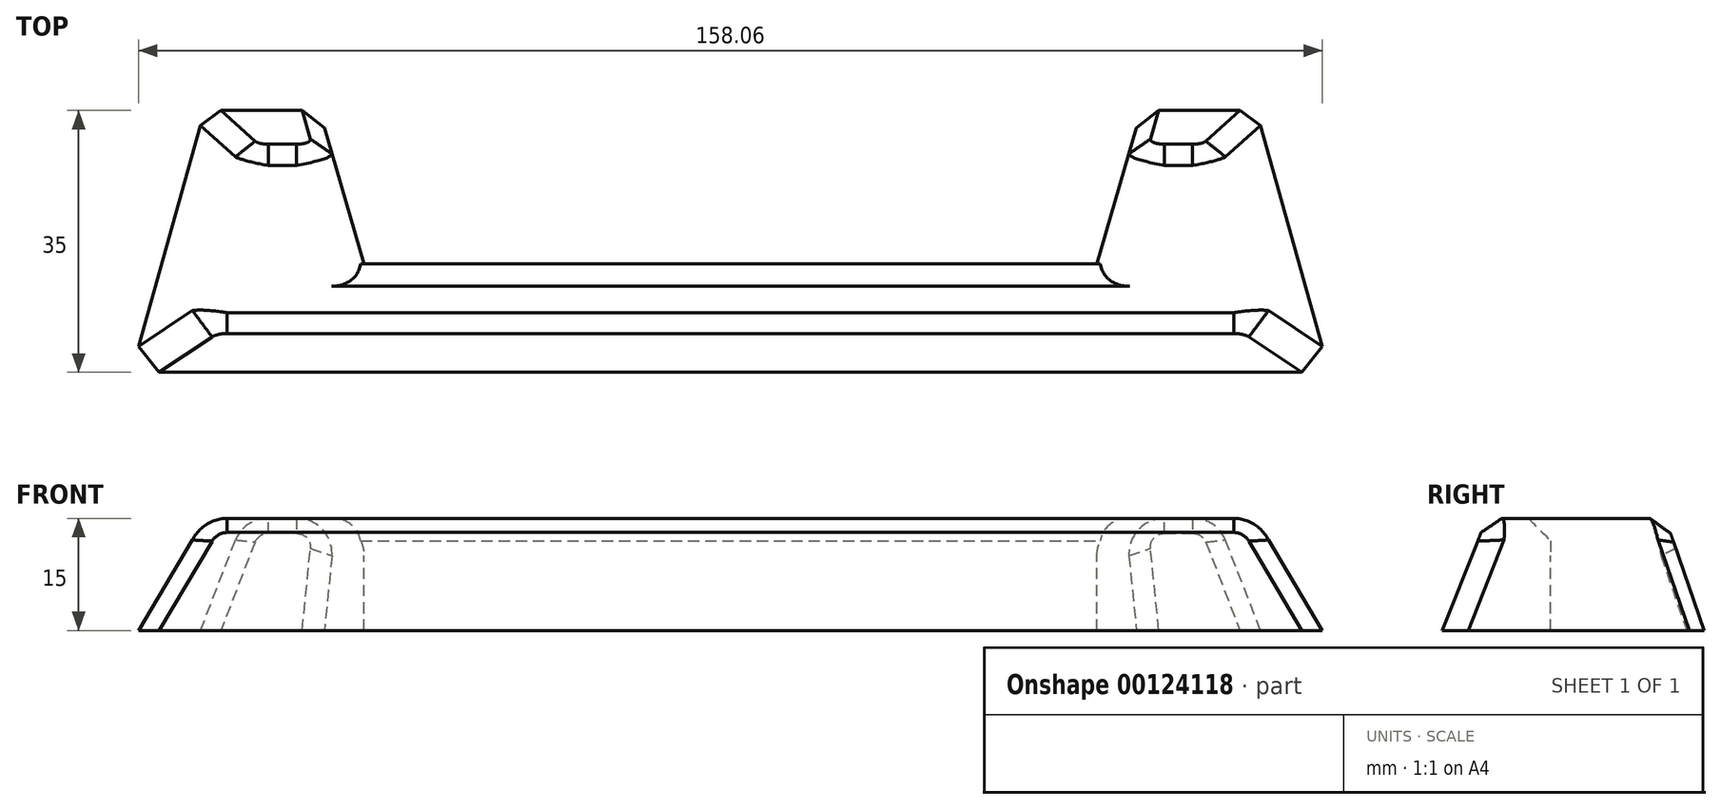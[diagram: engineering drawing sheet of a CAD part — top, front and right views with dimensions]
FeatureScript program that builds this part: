
annotation { "Feature Type Name" : "Feature", "Feature Type Description" : "" }
export const myFeature = defineFeature(function(context is Context, id is Id, definition is map)
    precondition{}
    {
        {
            var Q0;
            Q0=qCreatedBy(makeId("Top.planeOp"),FACE);
            var sketch = newSketch(context, id + "F0", { "sketchPlane" : qUnion([Q0])});
            skLineSegment(sketch, "E0", {"start": v(0, -14.5) * mm, "end": v(80, -14.5) * mm});
            skLineSegment(sketch, "E1", {"start": v(80, -14.5) * mm, "end": v(70.21, 20.5) * mm});
            skLineSegment(sketch, "E2", {"start": v(70.21, 20.5) * mm, "end": v(54.9, 20.5) * mm});
            skLineSegment(sketch, "E3", {"start": v(54.9, 20.5) * mm, "end": v(48.94, 0) * mm});
            skLineSegment(sketch, "E4", {"start": v(48.94, 0) * mm, "end": v(-31.06, 0) * mm});
            skLineSegment(sketch, "E5.MirrorCS", {"start": v(0, -14.5) * mm, "end": v(-80, -14.5) * mm});
            skLineSegment(sketch, "E6.MirrorCS", {"start": v(-80, -14.5) * mm, "end": v(-70.21, 20.5) * mm});
            skLineSegment(sketch, "E7.MirrorCS", {"start": v(-70.21, 20.5) * mm, "end": v(-54.9, 20.5) * mm});
            skLineSegment(sketch, "E8.MirrorCS", {"start": v(-48.94, 0) * mm, "end": v(0, 0) * mm});
            skLineSegment(sketch, "E9.MirrorCS", {"start": v(-54.9, 20.5) * mm, "end": v(-48.94, 0) * mm});
            skSolve(sketch);
        }
        {
            var Q0;
            Q0=qCreatedBy(makeId("Top.planeOp"),FACE);
            cPlane(context, id + "F1", {"entities" : qUnion([Q0]), "cplaneType" : CPlaneType.OFFSET, "offset" : 15 * mm, "width" : 152.4 * mm, "height" : 152.4 * mm});
        }
        {
            var Q0;
            Q0=qCreatedBy(id+"F1.planeOp",FACE);
            var sketch = newSketch(context, id + "F2", { "sketchPlane" : qUnion([Q0])});
            skLineSegment(sketch, "E10.3", {"start": v(53.38, 15.3) * mm, "end": v(48.94, 0) * mm});
            skLineSegment(sketch, "E10.4", {"start": v(48.94, 0) * mm, "end": v(0, 0) * mm});
            skLineSegment(sketch, "E11.2", {"start": v(64.42, 15.3) * mm, "end": v(53.38, 15.3) * mm});
            skLineSegment(sketch, "E11.3", {"start": v(71.09, -8.55) * mm, "end": v(64.42, 15.3) * mm});
            skPoint(sketch, "E10.7.end.orphan", {"position": v(-54.9, 20.5) * mm});
            skPoint(sketch, "E10.7.start.orphan", {"position": v(-70.21, 20.5) * mm});
            skPoint(sketch, "E10.8.end.orphan", {"position": v(-70.21, 20.5) * mm});
            skPoint(sketch, "E10.8.start.orphan", {"position": v(-80, -14.5) * mm});
            skPoint(sketch, "E10.9.end.orphan", {"position": v(-80, -14.5) * mm});
            skPoint(sketch, "E10.9.start.orphan", {"position": v(0, -14.5) * mm});
            skPoint(sketch, "E10.0.end.orphan", {"position": v(80, -14.5) * mm});
            skPoint(sketch, "E10.0.start.orphan", {"position": v(0, -14.5) * mm});
            skPoint(sketch, "E10.2.end.orphan", {"position": v(70.21, 20.5) * mm});
            skPoint(sketch, "E10.2.start.orphan", {"position": v(80, -14.5) * mm});
            skPoint(sketch, "E10.1.end.orphan", {"position": v(54.9, 20.5) * mm});
            skPoint(sketch, "E10.1.start.orphan", {"position": v(70.21, 20.5) * mm});
            skPoint(sketch, "E12.orphan", {"position": v(0, 0) * mm});
            skPoint(sketch, "E10.6.start.orphan", {"position": v(-48.94, 0) * mm});
            skPoint(sketch, "E13.orphan", {"position": v(-31.06, 0) * mm});
            skPoint(sketch, "E10.5.start.orphan", {"position": v(-54.9, 20.5) * mm});
            skLineSegment(sketch, "E14", {"start": v(71.09, -8.55) * mm, "end": v(0, -8.55) * mm});
            skLineSegment(sketch, "E15.MirrorCS", {"start": v(-71.09, -8.55) * mm, "end": v(0, -8.55) * mm});
            skLineSegment(sketch, "E16.MirrorCS", {"start": v(-71.09, -8.55) * mm, "end": v(-64.42, 15.3) * mm});
            skLineSegment(sketch, "E17.MirrorCS", {"start": v(-64.42, 15.3) * mm, "end": v(-53.38, 15.3) * mm});
            skLineSegment(sketch, "E18.MirrorCS", {"start": v(-48.94, 0) * mm, "end": v(0, 0) * mm});
            skLineSegment(sketch, "E19.MirrorCS", {"start": v(-53.38, 15.3) * mm, "end": v(-48.94, 0) * mm});
            skSolve(sketch);
        }
        {
            var Q0;
            Q0=makeQuery(id+"F0.imprint","IMPRINT",FACE,{"disambiguationData":[TD([[makeQuery(id+"F0.imprint","IMPRINT",EDGE,{"derivedFrom":sQuery(id+"F0.wireOp",EDGE,"E0")}),1.0]])]});
            var Q1;
            Q1=makeQuery(id+"F2.imprint","IMPRINT",FACE,{"disambiguationData":[TD([[makeQuery(id+"F2.imprint","IMPRINT",EDGE,{"derivedFrom":sQuery(id+"F2.wireOp",EDGE,"E10.3")}),1.0]])]});
            loft(context, id + "F3", {"sheetProfilesArray" : [{ "sheetProfileEntities" : qUnion([Q0]) }, { "sheetProfileEntities" : qUnion([Q1]) }]});
        }
        {
            var Q0;
            Q0=makeQuery(id+"F3.opLoft","MID_CAP_EDGE",EDGE,{"disambiguationData":[OSD([sQuery(id+"F2.wireOp",EDGE,"E15.MirrorCS"),sQuery(id+"F2.wireOp",EDGE,"E16.MirrorCS"),sQuery(id+"F2.wireOp",EDGE,"E17.MirrorCS")])],"capPos":1.0});
            var Q1;
            Q1=makeQuery(id+"F3.opLoft","MID_CAP_EDGE",EDGE,{"disambiguationData":[OSD([sQuery(id+"F2.wireOp",EDGE,"E17.MirrorCS"),sQuery(id+"F2.wireOp",EDGE,"E18.MirrorCS"),sQuery(id+"F2.wireOp",EDGE,"E19.MirrorCS")])],"capPos":1.0});
            var Q2;
            Q2=makeQuery(id+"F3.opLoft","MID_CAP_EDGE",EDGE,{"disambiguationData":[OSD([sQuery(id+"F2.wireOp",EDGE,"E10.3"),sQuery(id+"F2.wireOp",EDGE,"E10.4"),sQuery(id+"F2.wireOp",EDGE,"E11.2")])],"capPos":1.0});
            var Q3;
            Q3=makeQuery(id+"F3.opLoft","MID_CAP_EDGE",EDGE,{"disambiguationData":[OSD([sQuery(id+"F2.wireOp",EDGE,"E11.2"),sQuery(id+"F2.wireOp",EDGE,"E11.3"),sQuery(id+"F2.wireOp",EDGE,"E14")])],"capPos":1.0});
            fillet(context, id + "F4", {"entities" : qUnion([Q0, Q1, Q2, Q3]), "radius" : 5 * mm, "tangentPropagation" : true, "allowEdgeOverflow" : false});
        }
        {
            var Q0;
            Q0=makeQuery(id+"F3.opLoft","MID_CAP_EDGE",EDGE,{"disambiguationData":[OSD([sQuery(id+"F2.wireOp",EDGE,"E10.3"),sQuery(id+"F2.wireOp",EDGE,"E10.4"),sQuery(id+"F2.wireOp",EDGE,"E18.MirrorCS")])],"capPos":1.0});
            var Q1;
            Q1=makeQuery(id+"F3.opLoft","MID_CAP_EDGE",EDGE,{"disambiguationData":[OSD([sQuery(id+"F2.wireOp",EDGE,"E14"),sQuery(id+"F2.wireOp",EDGE,"E15.MirrorCS"),sQuery(id+"F2.wireOp",EDGE,"E16.MirrorCS")])],"capPos":1.0});
            chamfer(context, id + "F5", {"entities" : qUnion([Q0, Q1]), "width" : 3 * mm, "tangentPropagation" : true});
        }
        {
            var Q0;
            Q0=makeQuery(id+"F3.opLoft","SWEPT_EDGE",EDGE,{"disambiguationData":[OSD([sQuery(id+"F0.wireOp",EDGE,"E1"),sQuery(id+"F0.wireOp",EDGE,"E2"),sQuery(id+"F2.wireOp",EDGE,"E11.2"),sQuery(id+"F2.wireOp",EDGE,"E11.3")])]});
            var Q1;
            {var subQ0=sQuery(id+"F2.wireOp",EDGE,"E11.3");var subQ1=sQuery(id+"F2.wireOp",EDGE,"E11.2");Q1=makeQuery(id+"F4.opFillet","BLEND_EDGE",EDGE,{"blendedFrom":[makeQuery(id+"F3.opLoft","MID_CAP_EDGE",EDGE,{"disambiguationData":[OSD([subQ1,subQ0,sQuery(id+"F2.wireOp",EDGE,"E14")])],"capPos":1.0}),makeQuery(id+"F3.opLoft","SWEPT_FACE",FACE,{"disambiguationData":[OSD([sQuery(id+"F0.wireOp",EDGE,"E1"),sQuery(id+"F0.wireOp",EDGE,"E2"),sQuery(id+"F0.wireOp",EDGE,"E3"),sQuery(id+"F2.wireOp",EDGE,"E10.3"),subQ1,subQ0])]})],"blendedInto":[makeQuery(id+"F3.opLoft","SWEPT_FACE",FACE,{"disambiguationData":[OSD([sQuery(id+"F0.wireOp",EDGE,"E1"),sQuery(id+"F0.wireOp",EDGE,"E2"),sQuery(id+"F0.wireOp",EDGE,"E3"),sQuery(id+"F2.wireOp",EDGE,"E10.3"),subQ1,subQ0])]})]});}
            var Q2;
            {var subQ0=sQuery(id+"F2.wireOp",EDGE,"E11.2");var subQ1=sQuery(id+"F2.wireOp",EDGE,"E10.3");Q2=makeQuery(id+"F4.opFillet","BLEND_EDGE",EDGE,{"blendedFrom":[makeQuery(id+"F3.opLoft","MID_CAP_EDGE",EDGE,{"disambiguationData":[OSD([subQ1,sQuery(id+"F2.wireOp",EDGE,"E10.4"),subQ0])],"capPos":1.0}),makeQuery(id+"F3.opLoft","SWEPT_FACE",FACE,{"disambiguationData":[OSD([sQuery(id+"F0.wireOp",EDGE,"E1"),sQuery(id+"F0.wireOp",EDGE,"E2"),sQuery(id+"F0.wireOp",EDGE,"E3"),subQ1,subQ0,sQuery(id+"F2.wireOp",EDGE,"E11.3")])]})],"blendedInto":[makeQuery(id+"F3.opLoft","SWEPT_FACE",FACE,{"disambiguationData":[OSD([sQuery(id+"F0.wireOp",EDGE,"E1"),sQuery(id+"F0.wireOp",EDGE,"E2"),sQuery(id+"F0.wireOp",EDGE,"E3"),subQ1,subQ0,sQuery(id+"F2.wireOp",EDGE,"E11.3")])]})]});}
            var Q3;
            Q3=makeQuery(id+"F3.opLoft","SWEPT_EDGE",EDGE,{"disambiguationData":[OSD([sQuery(id+"F0.wireOp",EDGE,"E2"),sQuery(id+"F0.wireOp",EDGE,"E3"),sQuery(id+"F2.wireOp",EDGE,"E10.3"),sQuery(id+"F2.wireOp",EDGE,"E11.2")])]});
            var Q4;
            Q4=makeQuery(id+"F3.opLoft","MID_CAP_EDGE",EDGE,{"disambiguationData":[OSD([sQuery(id+"F2.wireOp",EDGE,"E10.3"),sQuery(id+"F2.wireOp",EDGE,"E11.2"),sQuery(id+"F2.wireOp",EDGE,"E11.3")])],"capPos":1.0});
            var Q5;
            Q5=makeQuery(id+"F3.opLoft","MID_CAP_EDGE",EDGE,{"disambiguationData":[OSD([sQuery(id+"F2.wireOp",EDGE,"E16.MirrorCS"),sQuery(id+"F2.wireOp",EDGE,"E17.MirrorCS"),sQuery(id+"F2.wireOp",EDGE,"E19.MirrorCS")])],"capPos":1.0});
            var Q6;
            {var subQ0=sQuery(id+"F2.wireOp",EDGE,"E19.MirrorCS");var subQ1=sQuery(id+"F2.wireOp",EDGE,"E17.MirrorCS");Q6=makeQuery(id+"F4.opFillet","BLEND_EDGE",EDGE,{"blendedFrom":[makeQuery(id+"F3.opLoft","MID_CAP_EDGE",EDGE,{"disambiguationData":[OSD([subQ1,sQuery(id+"F2.wireOp",EDGE,"E18.MirrorCS"),subQ0])],"capPos":1.0}),makeQuery(id+"F3.opLoft","SWEPT_FACE",FACE,{"disambiguationData":[OSD([sQuery(id+"F0.wireOp",EDGE,"E6.MirrorCS"),sQuery(id+"F0.wireOp",EDGE,"E7.MirrorCS"),sQuery(id+"F0.wireOp",EDGE,"E9.MirrorCS"),sQuery(id+"F2.wireOp",EDGE,"E16.MirrorCS"),subQ1,subQ0])]})],"blendedInto":[makeQuery(id+"F3.opLoft","SWEPT_FACE",FACE,{"disambiguationData":[OSD([sQuery(id+"F0.wireOp",EDGE,"E6.MirrorCS"),sQuery(id+"F0.wireOp",EDGE,"E7.MirrorCS"),sQuery(id+"F0.wireOp",EDGE,"E9.MirrorCS"),sQuery(id+"F2.wireOp",EDGE,"E16.MirrorCS"),subQ1,subQ0])]})]});}
            var Q7;
            {var subQ0=sQuery(id+"F2.wireOp",EDGE,"E17.MirrorCS");var subQ1=sQuery(id+"F2.wireOp",EDGE,"E16.MirrorCS");Q7=makeQuery(id+"F4.opFillet","BLEND_EDGE",EDGE,{"blendedFrom":[makeQuery(id+"F3.opLoft","MID_CAP_EDGE",EDGE,{"disambiguationData":[OSD([sQuery(id+"F2.wireOp",EDGE,"E15.MirrorCS"),subQ1,subQ0])],"capPos":1.0}),makeQuery(id+"F3.opLoft","SWEPT_FACE",FACE,{"disambiguationData":[OSD([sQuery(id+"F0.wireOp",EDGE,"E6.MirrorCS"),sQuery(id+"F0.wireOp",EDGE,"E7.MirrorCS"),sQuery(id+"F0.wireOp",EDGE,"E9.MirrorCS"),subQ1,subQ0,sQuery(id+"F2.wireOp",EDGE,"E19.MirrorCS")])]})],"blendedInto":[makeQuery(id+"F3.opLoft","SWEPT_FACE",FACE,{"disambiguationData":[OSD([sQuery(id+"F0.wireOp",EDGE,"E6.MirrorCS"),sQuery(id+"F0.wireOp",EDGE,"E7.MirrorCS"),sQuery(id+"F0.wireOp",EDGE,"E9.MirrorCS"),subQ1,subQ0,sQuery(id+"F2.wireOp",EDGE,"E19.MirrorCS")])]})]});}
            var Q8;
            Q8=makeQuery(id+"F3.opLoft","SWEPT_EDGE",EDGE,{"disambiguationData":[OSD([sQuery(id+"F0.wireOp",EDGE,"E6.MirrorCS"),sQuery(id+"F0.wireOp",EDGE,"E7.MirrorCS"),sQuery(id+"F2.wireOp",EDGE,"E16.MirrorCS"),sQuery(id+"F2.wireOp",EDGE,"E17.MirrorCS")])]});
            var Q9;
            Q9=makeQuery(id+"F3.opLoft","SWEPT_EDGE",EDGE,{"disambiguationData":[OSD([sQuery(id+"F0.wireOp",EDGE,"E7.MirrorCS"),sQuery(id+"F0.wireOp",EDGE,"E9.MirrorCS"),sQuery(id+"F2.wireOp",EDGE,"E17.MirrorCS"),sQuery(id+"F2.wireOp",EDGE,"E19.MirrorCS")])]});
            chamfer(context, id + "F6", {"entities" : qUnion([Q0, Q1, Q2, Q3, Q4, Q5, Q6, Q7, Q8, Q9]), "width" : 3 * mm, "tangentPropagation" : true});
        }
    });
